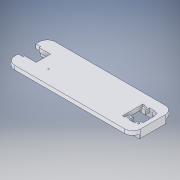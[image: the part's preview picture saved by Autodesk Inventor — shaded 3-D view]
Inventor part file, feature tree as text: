
AUTODESK INVENTOR PART (.ipt)
format: ipt  version: 2019 (Build 230136000, 136)  size: 265,728 bytes
history: native  units: mm
features: extrude x5, sketch x5, chamfer x1, fillet x1
ambient origin geometry x8: Origin, YZ Plane, XZ Plane, XY Plane, X Axis, Y Axis, Z Axis, Center Point
bodies: Solid1 (feature_tree)
feature tree (12):
  extrude  "Extrusion1"  Depth=50.0mm
  extrude  "Extrusion3"  Depth=8.0mm
  extrude  "Extrusion4"  Depth=70.0mm
  chamfer  "Chamfer1"  Distance=5.5mm
  extrude  "Extrusion5"  Depth=70.0mm
  extrude  "Extrusion6"  Depth=5.0mm TaperAngle=0.0deg
  fillet  "Fillet3"  Radius=5.0mm
  sketch  "Sketch1"  dims[d0=155.0mm d1=50.0mm]
  sketch  "Sketch3"  dims[d2=5.0mm d3=0.0mm d11=8.0mm]
  sketch  "Sketch4"  dims[d12=8.0mm d13=70.0mm]
  sketch  "Sketch6"  dims[d14=9.0mm]
  sketch  "Sketch8"  dims[d15=5.5mm d16=5.5mm d17=70.0mm d18=5.0mm d19=0.0mm d21=5.0mm d22=25.0mm d23=35.0mm d24=5.0mm d25=0.0mm d26=5.0mm d27=2.0mm d28=45.0deg d29=5.0mm d30=5.0mm d31=5.0mm d32=5.0mm d33=5.0mm d34=5.0mm d38=2.2mm d39=2.0mm d40=2.0mm d41=2.2mm d42=2.0mm d43=2.0mm d44=2.2mm d45=2.2mm d46=2.0mm d47=2.0mm d48=2.0mm d49=5.0mm d50=5.0mm d51=14.5mm d52=14.5mm d53=2.0mm d54=20.0mm d55=5.0mm d56=0.0mm d59=31.75mm d60=21.59mm d61=12.5mm d62=12.5mm d67=1.27mm d68=16.51mm d69=3.0mm d70=5.0mm d71=5.0mm d72=5.0mm d73=5.0mm d74=2.0mm d75=2.0mm d76=5.0mm d77=0.0mm d78=10.0mm d80=12.7mm]
